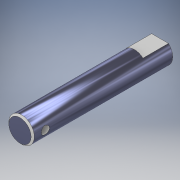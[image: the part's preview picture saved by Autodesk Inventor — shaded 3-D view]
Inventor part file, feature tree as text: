
AUTODESK INVENTOR PART (.ipt)
format: ipt  version: 2017 (Build 210142000, 142)  size: 130,560 bytes
history: native  units: mm
features: extrude x3, sketch x3, chamfer x1, plane x1
ambient origin geometry x8: Origin, YZ Plane, XZ Plane, XY Plane, X Axis, Y Axis, Z Axis, Center Point
bodies: Solid1 (feature_tree)
feature tree (8):
  extrude  "Extrusion1"  Depth=44.0mm TaperAngle=0.0deg
  chamfer  "Chamfer1"  Distance=0.5mm Angle=45.0deg
  extrude  "Extrusion2"  Depth=4.0mm
  plane  "Work Plane1"
  extrude  "Extrusion3"  Depth=4.0mm
  sketch  "Sketch2"  dims[d9=8.0mm d10=44.0mm d11=0.0mm d12=0.5mm d13=2.0mm d14=45.0deg]
  sketch  "Sketch3"  dims[d15=3.0mm d16=4.0mm]
  sketch  "Sketch4"  dims[d17=4.0mm d18=3.0mm d19=8.0mm d20=0.0mm d23=2.5mm d24=3.5mm d25=8.0mm d26=0.0mm]
